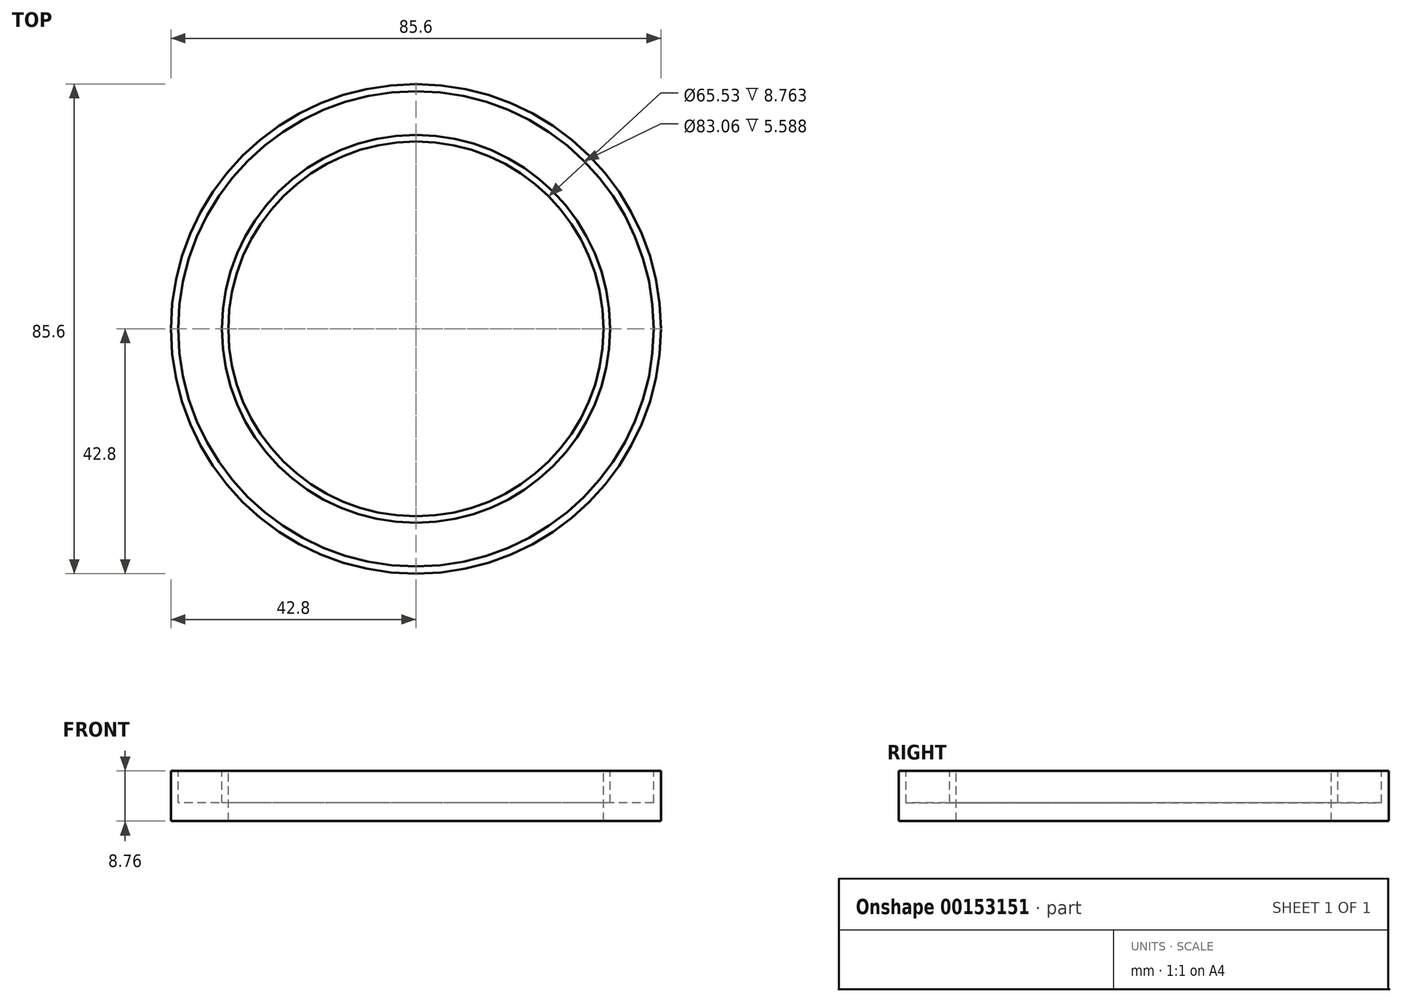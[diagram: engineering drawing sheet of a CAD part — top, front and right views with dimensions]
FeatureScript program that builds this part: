
annotation { "Feature Type Name" : "Feature", "Feature Type Description" : "" }
export const myFeature = defineFeature(function(context is Context, id is Id, definition is map)
    precondition{}
    {
        {
            var Q0;
            Q0=qCreatedBy(makeId("Front.planeOp"),FACE);
            var sketch = newSketch(context, id + "F0", { "sketchPlane" : qUnion([Q0])});
            skLineSegment(sketch, "E0", {"start": v(-30.93, 0) * mm, "end": v(28.88, 0) * mm, "construction": true});
            skLineSegment(sketch, "E1", {"start": v(32.77, 0) * mm, "end": v(32.77, -8.76) * mm});
            skLineSegment(sketch, "E2", {"start": v(32.77, -8.76) * mm, "end": v(42.8, -8.76) * mm});
            skLineSegment(sketch, "E3", {"start": v(42.8, -8.76) * mm, "end": v(42.8, 0) * mm});
            skLineSegment(sketch, "E4", {"start": v(42.8, 0) * mm, "end": v(41.53, 0) * mm});
            skLineSegment(sketch, "E5", {"start": v(41.53, 0) * mm, "end": v(41.53, -5.59) * mm});
            skLineSegment(sketch, "E6", {"start": v(41.53, -5.59) * mm, "end": v(33.9, -5.59) * mm});
            skLineSegment(sketch, "E7", {"start": v(33.9, -5.59) * mm, "end": v(33.9, 0) * mm});
            skLineSegment(sketch, "E8", {"start": v(33.9, 0) * mm, "end": v(32.77, 0) * mm});
            skLineSegment(sketch, "E9", {"start": v(41.6, 19.09) * mm, "end": v(41.6, -12.76) * mm, "construction": true});
            skLineSegment(sketch, "E10", {"start": v(0, 35.96) * mm, "end": v(0, -24.65) * mm, "construction": true});
            skSolve(sketch);
        }
        {
            var Q0;
            Q0 = qSketchRegion(id + "F0", true);
            var Q1;
            Q1=sQuery(id+"F0.wireOp",EDGE,"E10");
            revolve(context, id + "F1", {"entities" : qUnion([Q0]), "axis" : qUnion([Q1]), "revolveType" : RevolveType.FULL});
        }
    });
